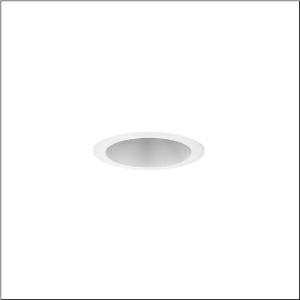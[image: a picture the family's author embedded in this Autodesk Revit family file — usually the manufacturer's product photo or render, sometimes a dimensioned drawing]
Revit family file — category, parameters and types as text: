
# Revit family: lunis_31-l_51dn15me41b
name_source: partatom
category: Lighting Fixtures
units: mm (PartAtom-declared; Revit-internal decimal feet)

## family parameters
Cut with Voids When Loaded = No
Host = Face
Light Source = No
Part Type = Normal
Room Calculation Point = No
Round Connector Dimension = Use Diameter
Shared = No

## types (1)
- --- (1 x LED, 1700 lm, 12 W, 4000K)
    Apparent Load = 12 VA
    CIE Flux Codes = 93 98 100 100 100
    Color Rendering = 80
    Color Temperature = 4000K
    Default Elevation = 1800 mm
    Description = Lunis 31-L, downlight, light control with reflector, light emission: direct distribution, LED rated luminous flux: 1.700lm, light colour: 840, mains connection: 220..240V, AC/DC, 0/50..60Hz, housing, of aluminium, white, protection rating (complete): IP20, protection rating (on room side): IP54, insulation class (complete): insulation class II (safety insulation), certification: CE, ENEC, packaging unit: 1 piece
    Height = 0 mm  [stored 0 ft]
    Lamp = 1 x LED
    Lamp Light Flux = 1700 lm
    Lamp Power = 12 W
    Lamp count = 1
    Length = 188 mm  [stored 0.616798 ft]
    Luminous efficacy = 142 lm/W
    Manufacturer = Siteco
    ModVariant = No
    Model = 51DN15ME41B
    Mounting Place = Ceiling
    Mounting Type = Recessed
    Number of Poles = 1
    OnlyDefault = Yes
    Power Factor = 1
    Product Name = Lunis 31-L
    Product group = downlight
    ProductGroupID = 401
    Protection Class = Protection class II
    Protection Degree = IP 20
    RLX_Detail_Level = 1
    RLX_Emergency_Light_Flux = 0 lm
    RLX_Emergency_Type = 0
    RLX_Emergency_Type_DB = No
    RlxData = <blob elided: 22181 chars, md5=701e0b30>
    Socket = socket
    Standby Power = 0 W
    System Light Flux = 1700 lm
    System Power = 12 W
    Type Comments = individual setting: luminous flux: 100 % | (OFF | ON) | 300 mA
    Type Image = l_1345911.jpg
    URL = http://relux.com
    VarID = @adj_031237
    Voltage = 0 V
    Weight = 0.00 kg
    Width = 0 mm  [stored 0 ft]

note: [stored X ft] marks values corroborated as IEEE doubles in the binary element streams (Revit-internal decimal feet)

## geometry (parser evidence)
native form markers: Blend x4, Sweep x12
no freeform markers — native parametric forms only
